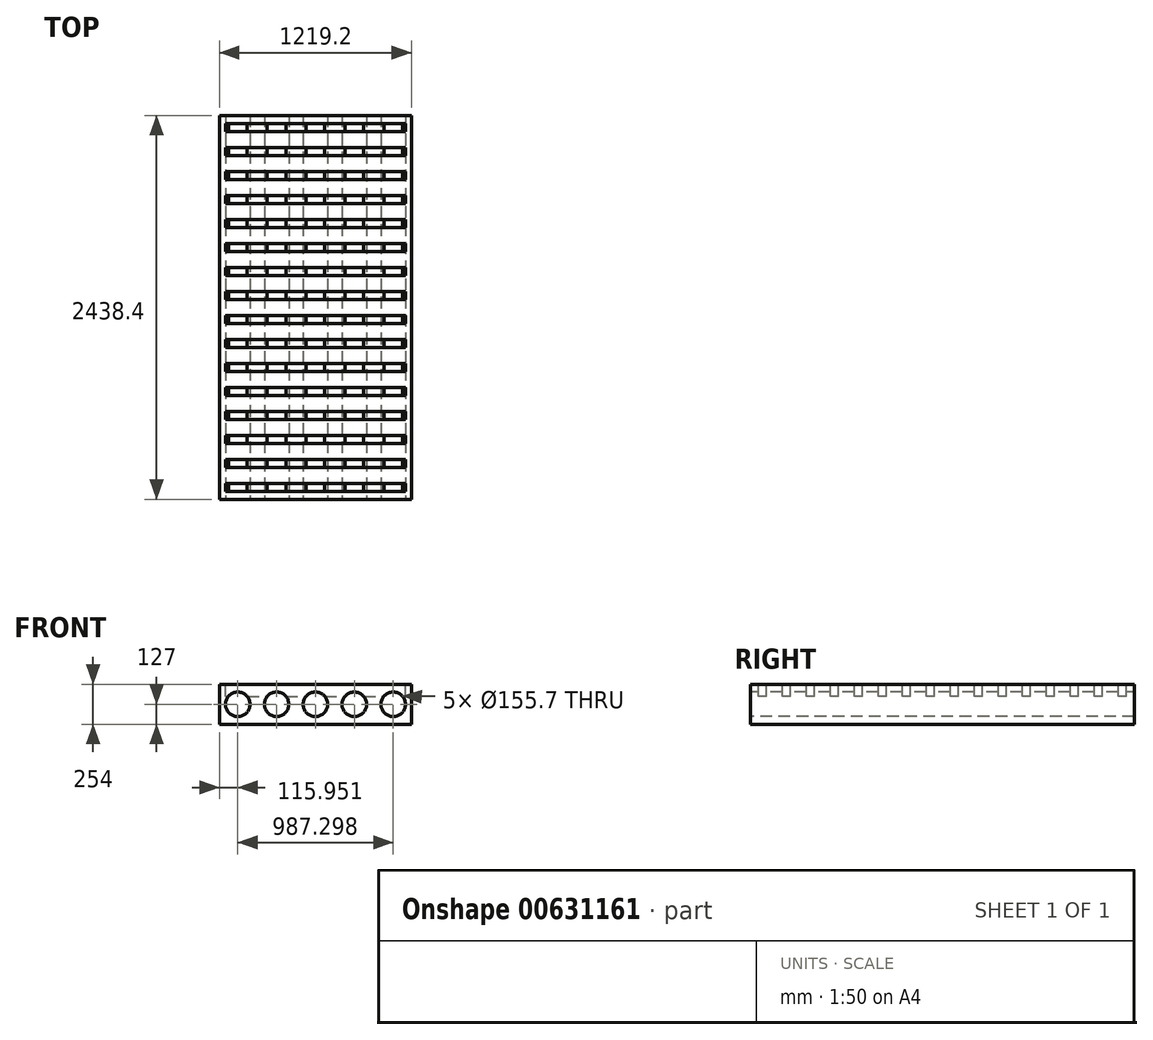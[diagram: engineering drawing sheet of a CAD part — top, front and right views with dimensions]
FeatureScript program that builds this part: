
annotation { "Feature Type Name" : "Feature", "Feature Type Description" : "" }
export const myFeature = defineFeature(function(context is Context, id is Id, definition is map)
    precondition{}
    {
        {
            var Q0;
            Q0=qCreatedBy(makeId("Top.planeOp"),FACE);
            var sketch = newSketch(context, id + "F0", { "sketchPlane" : qUnion([Q0])});
            skLineSegment(sketch, "E0.bottom", {"start": v(-609.6, 1219.2) * mm, "end": v(609.6, 1219.2) * mm});
            skLineSegment(sketch, "E0.top", {"start": v(-609.6, -1219.2) * mm, "end": v(609.6, -1219.2) * mm});
            skLineSegment(sketch, "E0.left", {"start": v(-609.6, 1219.2) * mm, "end": v(-609.6, -1219.2) * mm});
            skLineSegment(sketch, "E0.right", {"start": v(609.6, 1219.2) * mm, "end": v(609.6, -1219.2) * mm});
            skSolve(sketch);
        }
        {
            var Q0;
            Q0 = qSketchRegion(id + "F0", true);
            extrude(context, id + "F1", {"entities" : qUnion([Q0]), "depth" : 254 * mm, "offsetDistance" : 25.4 * mm});
        }
        {
            var Q0;
            Q0=makeQuery(id+"F1.opExtrude","SWEPT_FACE",FACE,{"disambiguationData":[OSD([sQuery(id+"F0.wireOp",EDGE,"E0.top")])]});
            var sketch = newSketch(context, id + "F2", { "sketchPlane" : qUnion([Q0])});
            skCircle(sketch, "E1", {"center": v(0, 127) * mm, "radius": 77.85 * mm});
            skCircle(sketch, "E2", {"center": v(493.65, 127) * mm, "radius": 77.85 * mm});
            skCircle(sketch, "E3", {"center": v(-493.65, 127) * mm, "radius": 77.85 * mm});
            skCircle(sketch, "E4", {"center": v(-246.82, 127) * mm, "radius": 77.85 * mm});
            skCircle(sketch, "E5", {"center": v(246.82, 127) * mm, "radius": 77.85 * mm});
            skLineSegment(sketch, "E6", {"start": v(0, 127) * mm, "end": v(493.65, 127) * mm, "construction": true});
            skLineSegment(sketch, "E7", {"start": v(-493.65, 127) * mm, "end": v(0, 127) * mm, "construction": true});
            skSolve(sketch);
        }
        {
            var Q0;
            Q0 = qSketchRegion(id + "F2", true);
            extrude(context, id + "F3", {"entities" : qUnion([Q0]), "operationType" : NewBodyOperationType.REMOVE, "endBound" : BoundingType.THROUGH_ALL, "oppositeDirection" : true, "depth" : 25.4 * mm, "offsetDistance" : 25.4 * mm});
        }
        {
            var Q0;
            Q0=makeQuery(id+"F1.opExtrude","CAP_FACE",FACE,{"disambiguationData":[OSD([sQuery(id+"F0.wireOp",EDGE,"E0.bottom"),sQuery(id+"F0.wireOp",EDGE,"E0.top"),sQuery(id+"F0.wireOp",EDGE,"E0.left"),sQuery(id+"F0.wireOp",EDGE,"E0.right")])],"isStart":false});
            var sketch = newSketch(context, id + "F4", { "sketchPlane" : qUnion([Q0])});
            skLineSegment(sketch, "E8.bottom", {"start": v(-571.25, -1168.4) * mm, "end": v(571.25, -1168.4) * mm});
            skLineSegment(sketch, "E8.top", {"start": v(-571.25, -1117.6) * mm, "end": v(571.25, -1117.6) * mm});
            skLineSegment(sketch, "E8.left", {"start": v(-571.25, -1168.4) * mm, "end": v(-571.25, -1117.6) * mm});
            skLineSegment(sketch, "E8.right", {"start": v(571.25, -1168.4) * mm, "end": v(571.25, -1117.6) * mm});
            skLineSegment(sketch, "E9.0.1.0", {"start": v(-571.25, -1016) * mm, "end": v(571.25, -1016) * mm});
            skLineSegment(sketch, "E9.0.1.1", {"start": v(571.25, -1016) * mm, "end": v(571.25, -965.2) * mm});
            skLineSegment(sketch, "E9.0.1.2", {"start": v(-571.25, -1016) * mm, "end": v(-571.25, -965.2) * mm});
            skLineSegment(sketch, "E9.0.1.3", {"start": v(-571.25, -965.2) * mm, "end": v(571.25, -965.2) * mm});
            skLineSegment(sketch, "E9.0.2.0", {"start": v(-571.25, -863.6) * mm, "end": v(571.25, -863.6) * mm});
            skLineSegment(sketch, "E9.0.2.1", {"start": v(571.25, -863.6) * mm, "end": v(571.25, -812.8) * mm});
            skLineSegment(sketch, "E9.0.2.2", {"start": v(-571.25, -863.6) * mm, "end": v(-571.25, -812.8) * mm});
            skLineSegment(sketch, "E9.0.2.3", {"start": v(-571.25, -812.8) * mm, "end": v(571.25, -812.8) * mm});
            skLineSegment(sketch, "E9.0.3.0", {"start": v(-571.25, -711.2) * mm, "end": v(571.25, -711.2) * mm});
            skLineSegment(sketch, "E9.0.3.1", {"start": v(571.25, -711.2) * mm, "end": v(571.25, -660.4) * mm});
            skLineSegment(sketch, "E9.0.3.2", {"start": v(-571.25, -711.2) * mm, "end": v(-571.25, -660.4) * mm});
            skLineSegment(sketch, "E9.0.3.3", {"start": v(-571.25, -660.4) * mm, "end": v(571.25, -660.4) * mm});
            skLineSegment(sketch, "E9.0.4.0", {"start": v(-571.25, -558.8) * mm, "end": v(571.25, -558.8) * mm});
            skLineSegment(sketch, "E9.0.4.1", {"start": v(571.25, -558.8) * mm, "end": v(571.25, -508) * mm});
            skLineSegment(sketch, "E9.0.4.2", {"start": v(-571.25, -558.8) * mm, "end": v(-571.25, -508) * mm});
            skLineSegment(sketch, "E9.0.4.3", {"start": v(-571.25, -508) * mm, "end": v(571.25, -508) * mm});
            skLineSegment(sketch, "E9.0.5.0", {"start": v(-571.25, -406.4) * mm, "end": v(571.25, -406.4) * mm});
            skLineSegment(sketch, "E9.0.5.1", {"start": v(571.25, -406.4) * mm, "end": v(571.25, -355.6) * mm});
            skLineSegment(sketch, "E9.0.5.2", {"start": v(-571.25, -406.4) * mm, "end": v(-571.25, -355.6) * mm});
            skLineSegment(sketch, "E9.0.5.3", {"start": v(-571.25, -355.6) * mm, "end": v(571.25, -355.6) * mm});
            skLineSegment(sketch, "E9.0.6.0", {"start": v(-571.25, -254) * mm, "end": v(571.25, -254) * mm});
            skLineSegment(sketch, "E9.0.6.1", {"start": v(571.25, -254) * mm, "end": v(571.25, -203.2) * mm});
            skLineSegment(sketch, "E9.0.6.2", {"start": v(-571.25, -254) * mm, "end": v(-571.25, -203.2) * mm});
            skLineSegment(sketch, "E9.0.6.3", {"start": v(-571.25, -203.2) * mm, "end": v(571.25, -203.2) * mm});
            skLineSegment(sketch, "E9.0.7.0", {"start": v(-571.25, -101.6) * mm, "end": v(571.25, -101.6) * mm});
            skLineSegment(sketch, "E9.0.7.1", {"start": v(571.25, -101.6) * mm, "end": v(571.25, -50.8) * mm});
            skLineSegment(sketch, "E9.0.7.2", {"start": v(-571.25, -101.6) * mm, "end": v(-571.25, -50.8) * mm});
            skLineSegment(sketch, "E9.0.7.3", {"start": v(-571.25, -50.8) * mm, "end": v(571.25, -50.8) * mm});
            skLineSegment(sketch, "E9.0.8.0", {"start": v(-571.25, 50.8) * mm, "end": v(571.25, 50.8) * mm});
            skLineSegment(sketch, "E9.0.8.1", {"start": v(571.25, 50.8) * mm, "end": v(571.25, 101.6) * mm});
            skLineSegment(sketch, "E9.0.8.2", {"start": v(-571.25, 50.8) * mm, "end": v(-571.25, 101.6) * mm});
            skLineSegment(sketch, "E9.0.8.3", {"start": v(-571.25, 101.6) * mm, "end": v(571.25, 101.6) * mm});
            skLineSegment(sketch, "E9.0.9.0", {"start": v(-571.25, 203.2) * mm, "end": v(571.25, 203.2) * mm});
            skLineSegment(sketch, "E9.0.9.1", {"start": v(571.25, 203.2) * mm, "end": v(571.25, 254) * mm});
            skLineSegment(sketch, "E9.0.9.2", {"start": v(-571.25, 203.2) * mm, "end": v(-571.25, 254) * mm});
            skLineSegment(sketch, "E9.0.9.3", {"start": v(-571.25, 254) * mm, "end": v(571.25, 254) * mm});
            skLineSegment(sketch, "E9.0.10.0", {"start": v(-571.25, 355.6) * mm, "end": v(571.25, 355.6) * mm});
            skLineSegment(sketch, "E9.0.10.1", {"start": v(571.25, 355.6) * mm, "end": v(571.25, 406.4) * mm});
            skLineSegment(sketch, "E9.0.10.2", {"start": v(-571.25, 355.6) * mm, "end": v(-571.25, 406.4) * mm});
            skLineSegment(sketch, "E9.0.10.3", {"start": v(-571.25, 406.4) * mm, "end": v(571.25, 406.4) * mm});
            skLineSegment(sketch, "E9.0.11.0", {"start": v(-571.25, 508) * mm, "end": v(571.25, 508) * mm});
            skLineSegment(sketch, "E9.0.11.1", {"start": v(571.25, 508) * mm, "end": v(571.25, 558.8) * mm});
            skLineSegment(sketch, "E9.0.11.2", {"start": v(-571.25, 508) * mm, "end": v(-571.25, 558.8) * mm});
            skLineSegment(sketch, "E9.0.11.3", {"start": v(-571.25, 558.8) * mm, "end": v(571.25, 558.8) * mm});
            skLineSegment(sketch, "E9.0.12.0", {"start": v(-571.25, 660.4) * mm, "end": v(571.25, 660.4) * mm});
            skLineSegment(sketch, "E9.0.12.1", {"start": v(571.25, 660.4) * mm, "end": v(571.25, 711.2) * mm});
            skLineSegment(sketch, "E9.0.12.2", {"start": v(-571.25, 660.4) * mm, "end": v(-571.25, 711.2) * mm});
            skLineSegment(sketch, "E9.0.12.3", {"start": v(-571.25, 711.2) * mm, "end": v(571.25, 711.2) * mm});
            skLineSegment(sketch, "E9.0.13.0", {"start": v(-571.25, 812.8) * mm, "end": v(571.25, 812.8) * mm});
            skLineSegment(sketch, "E9.0.13.1", {"start": v(571.25, 812.8) * mm, "end": v(571.25, 863.6) * mm});
            skLineSegment(sketch, "E9.0.13.2", {"start": v(-571.25, 812.8) * mm, "end": v(-571.25, 863.6) * mm});
            skLineSegment(sketch, "E9.0.13.3", {"start": v(-571.25, 863.6) * mm, "end": v(571.25, 863.6) * mm});
            skLineSegment(sketch, "E9.0.14.0", {"start": v(-571.25, 965.2) * mm, "end": v(571.25, 965.2) * mm});
            skLineSegment(sketch, "E9.0.14.1", {"start": v(571.25, 965.2) * mm, "end": v(571.25, 1016) * mm});
            skLineSegment(sketch, "E9.0.14.2", {"start": v(-571.25, 965.2) * mm, "end": v(-571.25, 1016) * mm});
            skLineSegment(sketch, "E9.0.14.3", {"start": v(-571.25, 1016) * mm, "end": v(571.25, 1016) * mm});
            skLineSegment(sketch, "E9.0.15.0", {"start": v(-571.25, 1117.6) * mm, "end": v(571.25, 1117.6) * mm});
            skLineSegment(sketch, "E9.0.15.1", {"start": v(571.25, 1117.6) * mm, "end": v(571.25, 1168.4) * mm});
            skLineSegment(sketch, "E9.0.15.2", {"start": v(-571.25, 1117.6) * mm, "end": v(-571.25, 1168.4) * mm});
            skLineSegment(sketch, "E9.0.15.3", {"start": v(-571.25, 1168.4) * mm, "end": v(571.25, 1168.4) * mm});
            skLineSegment(sketch, "E9.direction1", {"start": v(-571.25, -1168.4) * mm, "end": v(-545.85, -1168.4) * mm, "construction": true});
            skLineSegment(sketch, "E9.direction2", {"start": v(-571.25, -1168.4) * mm, "end": v(-571.25, -1016) * mm, "construction": true});
            skSolve(sketch);
        }
        {
            var Q0;
            Q0 = qSketchRegion(id + "F4", true);
            extrude(context, id + "F5", {"entities" : qUnion([Q0]), "operationType" : NewBodyOperationType.REMOVE, "oppositeDirection" : true, "depth" : 76.2 * mm, "offsetDistance" : 25.4 * mm});
        }
    });
